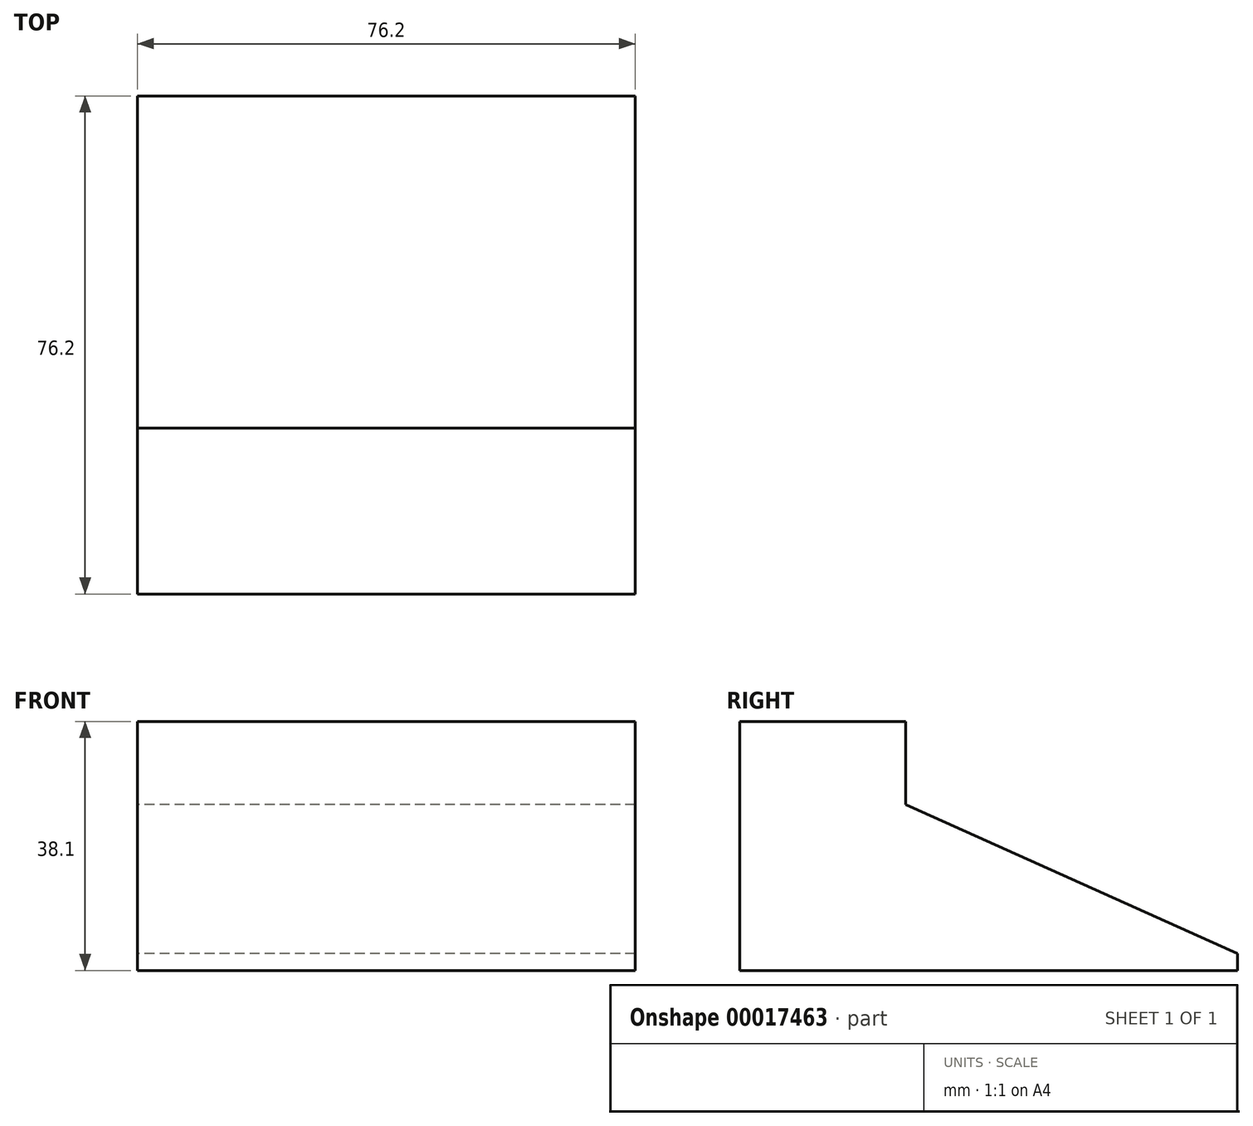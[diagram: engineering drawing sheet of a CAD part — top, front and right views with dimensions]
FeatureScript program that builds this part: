
annotation { "Feature Type Name" : "Feature", "Feature Type Description" : "" }
export const myFeature = defineFeature(function(context is Context, id is Id, definition is map)
    precondition{}
    {
        {
            var Q0;
            Q0=qCreatedBy(makeId("Right.planeOp"),FACE);
            var sketch = newSketch(context, id + "F0", { "sketchPlane" : qUnion([Q0])});
            skLineSegment(sketch, "E0", {"start": v(-25.4, 7.87) * mm, "end": v(-25.4, -30.23) * mm});
            skLineSegment(sketch, "E1", {"start": v(-25.4, -30.23) * mm, "end": v(50.8, -30.23) * mm});
            skLineSegment(sketch, "E2", {"start": v(50.8, -30.23) * mm, "end": v(50.8, -27.66) * mm});
            skLineSegment(sketch, "E3", {"start": v(50.8, -27.66) * mm, "end": v(0, -4.83) * mm});
            skLineSegment(sketch, "E4", {"start": v(0, -4.83) * mm, "end": v(0, 7.87) * mm});
            skLineSegment(sketch, "E5", {"start": v(0, 7.87) * mm, "end": v(-25.4, 7.87) * mm});
            skSolve(sketch);
        }
        {
            var Q0;
            Q0=makeQuery(id+"F0.imprint","IMPRINT",FACE,{"disambiguationData":[TD([[makeQuery(id+"F0.imprint","IMPRINT",EDGE,{"derivedFrom":sQuery(id+"F0.wireOp",EDGE,"E0")}),1.0]])]});
            extrude(context, id + "F1", {"entities" : qUnion([Q0]), "depth" : 76.2 * mm});
        }
    });
